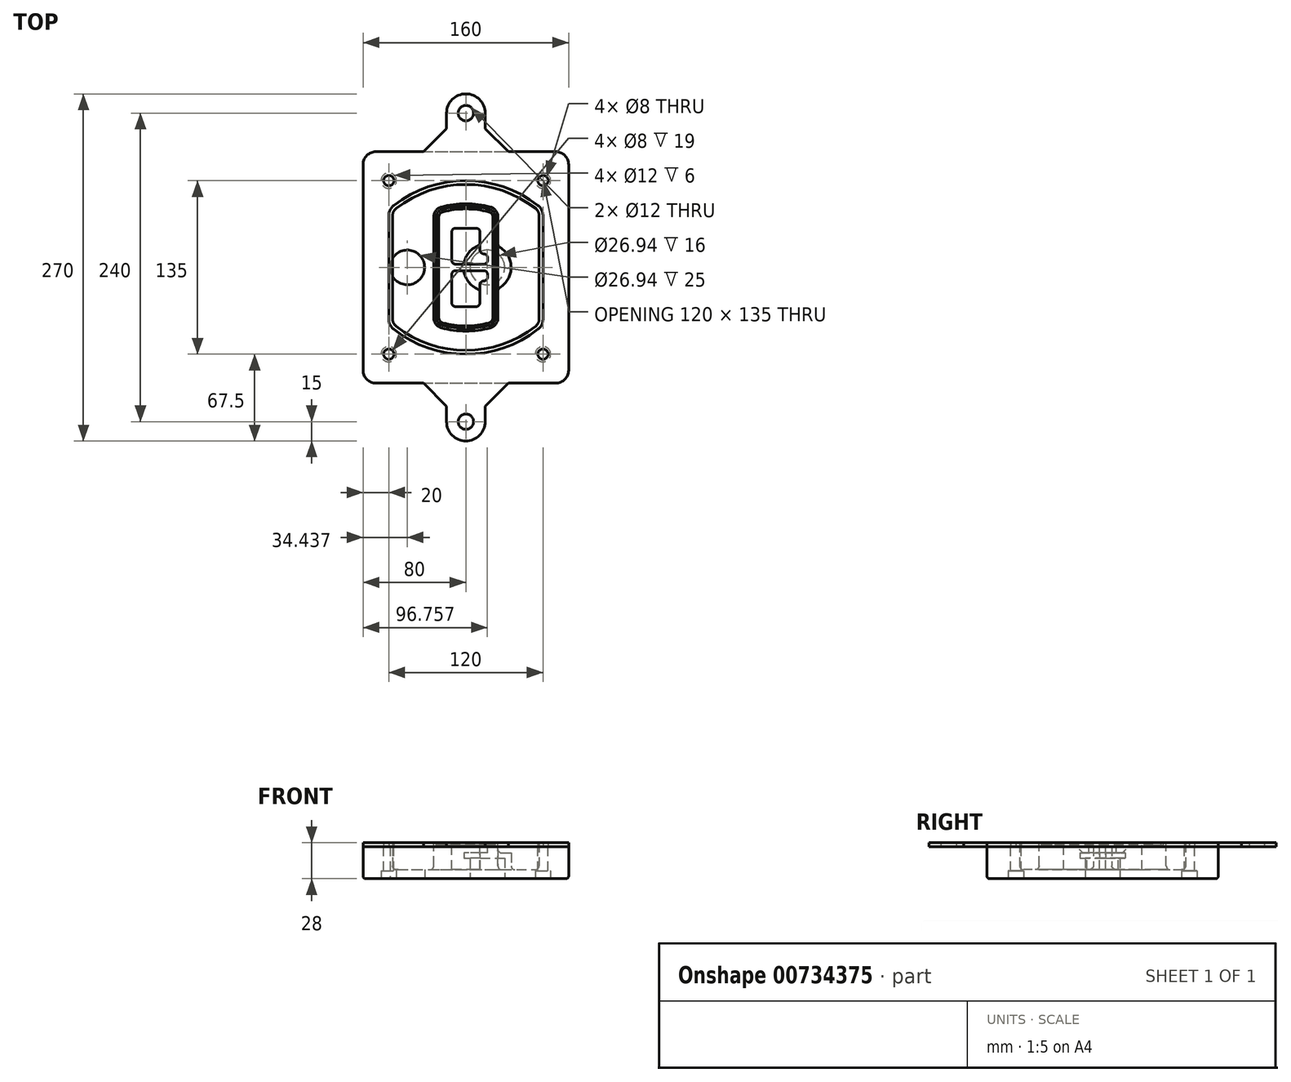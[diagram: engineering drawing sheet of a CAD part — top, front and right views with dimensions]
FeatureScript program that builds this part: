
annotation { "Feature Type Name" : "Feature", "Feature Type Description" : "" }
export const myFeature = defineFeature(function(context is Context, id is Id, definition is map)
    precondition{}
    {
        {
            var Q0;
            Q0=qCreatedBy(makeId("Top.planeOp"),FACE);
            var sketch = newSketch(context, id + "F0", { "sketchPlane" : qUnion([Q0])});
            skPoint(sketch, "E0.rect.middle", {"position": v(0, 0) * mm});
            skLineSegment(sketch, "E1.bottom", {"start": v(-70, -90) * mm, "end": v(70, -90) * mm});
            skLineSegment(sketch, "E1.top", {"start": v(-70, 90) * mm, "end": v(70, 90) * mm});
            skLineSegment(sketch, "E1.left", {"start": v(-80, -80) * mm, "end": v(-80, 80) * mm});
            skLineSegment(sketch, "E1.right", {"start": v(80, -80) * mm, "end": v(80, 80) * mm});
            skLineSegment(sketch, "E2", {"start": v(-80, 90) * mm, "end": v(80, -90) * mm, "construction": true});
            skLineSegment(sketch, "E3", {"start": v(80, 90) * mm, "end": v(-80, -90) * mm, "construction": true});
            skCircle(sketch, "E4", {"center": v(-60, 67.5) * mm, "radius": 4 * mm});
            skCircle(sketch, "E5", {"center": v(60, 67.5) * mm, "radius": 4 * mm});
            skCircle(sketch, "E6", {"center": v(60, -67.5) * mm, "radius": 4 * mm});
            skCircle(sketch, "E7", {"center": v(-60, -67.5) * mm, "radius": 4 * mm});
            skLineSegment(sketch, "E8", {"start": v(-60, 67.5) * mm, "end": v(60, 67.5) * mm, "construction": true});
            skLineSegment(sketch, "E9", {"start": v(60, 67.5) * mm, "end": v(60, -67.5) * mm, "construction": true});
            skLineSegment(sketch, "E10", {"start": v(60, -67.5) * mm, "end": v(-60, -67.5) * mm, "construction": true});
            skLineSegment(sketch, "E11", {"start": v(-60, -67.5) * mm, "end": v(-60, 67.5) * mm, "construction": true});
            skLineSegment(sketch, "E12", {"start": v(-60, 40.3) * mm, "end": v(-60, -40.3) * mm});
            skLineSegment(sketch, "E13", {"start": v(60, 40.3) * mm, "end": v(60, -40.3) * mm});
            skArc(sketch, "E14", {"start": v(56.15, 48.18) * mm, "mid": v(0, 67.5) * mm, "end": v(-56.15, 48.18) * mm});
            skArc(sketch, "E15", {"start": v(-56.15, -48.18) * mm, "mid": v(0, -67.5) * mm, "end": v(56.15, -48.18) * mm});
            skLineSegment(sketch, "E16", {"start": v(-60, 0) * mm, "end": v(60, 0) * mm, "construction": true});
            skPoint(sketch, "E17.visualSharp", {"position": v(-60, -45) * mm});
            skArc(sketch, "E17.filletArc", {"start": v(-60, -40.3) * mm, "mid": v(-58.99, -44.68) * mm, "end": v(-56.15, -48.18) * mm});
            skPoint(sketch, "E18.visualSharp", {"position": v(-60, 45) * mm});
            skArc(sketch, "E18.filletArc", {"start": v(-56.15, 48.18) * mm, "mid": v(-58.99, 44.68) * mm, "end": v(-60, 40.3) * mm});
            skPoint(sketch, "E19.visualSharp", {"position": v(60, 45) * mm});
            skArc(sketch, "E19.filletArc", {"start": v(60, 40.3) * mm, "mid": v(58.99, 44.68) * mm, "end": v(56.15, 48.18) * mm});
            skPoint(sketch, "E20.visualSharp", {"position": v(60, -45) * mm});
            skArc(sketch, "E20.filletArc", {"start": v(56.15, -48.18) * mm, "mid": v(58.99, -44.68) * mm, "end": v(60, -40.3) * mm});
            skPoint(sketch, "E21.visualSharp", {"position": v(-80, 90) * mm});
            skArc(sketch, "E21.filletArc", {"start": v(-70, 90) * mm, "mid": v(-77.07, 87.07) * mm, "end": v(-80, 80) * mm});
            skPoint(sketch, "E22.visualSharp", {"position": v(80, 90) * mm});
            skArc(sketch, "E22.filletArc", {"start": v(80, 80) * mm, "mid": v(77.07, 87.07) * mm, "end": v(70, 90) * mm});
            skPoint(sketch, "E23.visualSharp", {"position": v(80, -90) * mm});
            skArc(sketch, "E23.filletArc", {"start": v(70, -90) * mm, "mid": v(77.07, -87.07) * mm, "end": v(80, -80) * mm});
            skPoint(sketch, "E24.visualSharp", {"position": v(-80, -90) * mm});
            skArc(sketch, "E24.filletArc", {"start": v(-80, -80) * mm, "mid": v(-77.07, -87.07) * mm, "end": v(-70, -90) * mm});
            skArc(sketch, "E25.0", {"start": v(57, 40.3) * mm, "mid": v(56.3, 43.36) * mm, "end": v(54.3, 45.81) * mm});
            skLineSegment(sketch, "E25.1", {"start": v(57, 40.3) * mm, "end": v(57, -40.3) * mm});
            skArc(sketch, "E25.2", {"start": v(54.3, -45.81) * mm, "mid": v(56.3, -43.36) * mm, "end": v(57, -40.3) * mm});
            skArc(sketch, "E25.3", {"start": v(-54.3, -45.81) * mm, "mid": v(0, -64.5) * mm, "end": v(54.3, -45.81) * mm});
            skArc(sketch, "E25.4", {"start": v(-57, -40.3) * mm, "mid": v(-56.3, -43.36) * mm, "end": v(-54.3, -45.81) * mm});
            skArc(sketch, "E25.5", {"start": v(54.3, 45.81) * mm, "mid": v(0, 64.5) * mm, "end": v(-54.3, 45.81) * mm});
            skLineSegment(sketch, "E25.6", {"start": v(-57, 40.3) * mm, "end": v(-57, -40.3) * mm});
            skArc(sketch, "E25.7", {"start": v(-54.3, 45.81) * mm, "mid": v(-56.3, 43.36) * mm, "end": v(-57, 40.3) * mm});
            skArc(sketch, "E26.0", {"start": v(-58.62, 51.33) * mm, "mid": v(-62.58, 46.43) * mm, "end": v(-64, 40.3) * mm});
            skArc(sketch, "E26.1", {"start": v(58.62, 51.33) * mm, "mid": v(0, 71.5) * mm, "end": v(-58.62, 51.33) * mm});
            skArc(sketch, "E26.2", {"start": v(64, 40.3) * mm, "mid": v(62.58, 46.43) * mm, "end": v(58.62, 51.33) * mm});
            skLineSegment(sketch, "E26.3", {"start": v(64, 40.3) * mm, "end": v(64, -40.3) * mm});
            skArc(sketch, "E26.4", {"start": v(58.62, -51.33) * mm, "mid": v(62.58, -46.43) * mm, "end": v(64, -40.3) * mm});
            skLineSegment(sketch, "E26.5", {"start": v(-64, 40.3) * mm, "end": v(-64, -40.3) * mm});
            skArc(sketch, "E26.6", {"start": v(-58.62, -51.33) * mm, "mid": v(0, -71.5) * mm, "end": v(58.62, -51.33) * mm});
            skArc(sketch, "E26.7", {"start": v(-64, -40.3) * mm, "mid": v(-62.58, -46.43) * mm, "end": v(-58.62, -51.33) * mm});
            skSolve(sketch);
        }
        {
            var Q0;
            Q0=makeQuery(id+"F0.imprint","IMPRINT",FACE,{"disambiguationData":[TD([[makeQuery(id+"F0.imprint","IMPRINT",EDGE,{"derivedFrom":sQuery(id+"F0.wireOp",EDGE,"E1.bottom")}),1.0]])]});
            var Q1;
            Q1=makeQuery(id+"F0.imprint","IMPRINT",FACE,{"disambiguationData":[TD([[makeQuery(id+"F0.imprint","IMPRINT",EDGE,{"derivedFrom":sQuery(id+"F0.wireOp",EDGE,"E12")}),1.0]])]});
            var Q2;
            Q2=makeQuery(id+"F0.imprint","IMPRINT",FACE,{"disambiguationData":[TD([[makeQuery(id+"F0.imprint","IMPRINT",EDGE,{"derivedFrom":sQuery(id+"F0.wireOp",EDGE,"E25.0")}),1.0]])]});
            var Q3;
            Q3=makeQuery(id+"F0.imprint","IMPRINT",FACE,{"disambiguationData":[TD([[makeQuery(id+"F0.imprint","IMPRINT",EDGE,{"derivedFrom":sQuery(id+"F0.wireOp",EDGE,"E12")}),-1.0]])]});
            extrude(context, id + "F1", {"entities" : qUnion([Q0, Q1, Q2, Q3]), "oppositeDirection" : true, "depth" : 25 * mm});
        }
        {
            var Q0;
            Q0=makeQuery(id+"F0.imprint","IMPRINT",FACE,{"disambiguationData":[TD([[makeQuery(id+"F0.imprint","IMPRINT",EDGE,{"derivedFrom":sQuery(id+"F0.wireOp",EDGE,"E12")}),1.0]])]});
            extrude(context, id + "F2", {"entities" : qUnion([Q0]), "operationType" : NewBodyOperationType.ADD, "depth" : 3 * mm});
        }
        {
            var Q0;
            Q0=makeQuery(id+"F0.imprint","IMPRINT",FACE,{"disambiguationData":[TD([[makeQuery(id+"F0.imprint","IMPRINT",EDGE,{"derivedFrom":sQuery(id+"F0.wireOp",EDGE,"E25.0")}),1.0]])]});
            extrude(context, id + "F3", {"entities" : qUnion([Q0]), "operationType" : NewBodyOperationType.REMOVE, "oppositeDirection" : true, "depth" : 18 * mm});
        }
        {
            var Q0;
            Q0=makeQuery(id+"F2.opExtrude","CAP_FACE",FACE,{"disambiguationData":[OSD([sQuery(id+"F0.wireOp",EDGE,"E12"),sQuery(id+"F0.wireOp",EDGE,"E13"),sQuery(id+"F0.wireOp",EDGE,"E14"),sQuery(id+"F0.wireOp",EDGE,"E15"),sQuery(id+"F0.wireOp",EDGE,"E17.filletArc"),sQuery(id+"F0.wireOp",EDGE,"E18.filletArc"),sQuery(id+"F0.wireOp",EDGE,"E19.filletArc"),sQuery(id+"F0.wireOp",EDGE,"E20.filletArc"),sQuery(id+"F0.wireOp",EDGE,"E25.0"),sQuery(id+"F0.wireOp",EDGE,"E25.1"),sQuery(id+"F0.wireOp",EDGE,"E25.2"),sQuery(id+"F0.wireOp",EDGE,"E25.3"),sQuery(id+"F0.wireOp",EDGE,"E25.4"),sQuery(id+"F0.wireOp",EDGE,"E25.5"),sQuery(id+"F0.wireOp",EDGE,"E25.6"),sQuery(id+"F0.wireOp",EDGE,"E25.7")])],"isStart":false});
            var sketch = newSketch(context, id + "F4", { "sketchPlane" : qUnion([Q0])});
            skArc(sketch, "E27.0", {"start": v(-19.08, -46.97) * mm, "mid": v(0, -49.5) * mm, "end": v(19.08, -46.97) * mm});
            skArc(sketch, "E28.0", {"start": v(19.08, 46.97) * mm, "mid": v(0, 49.5) * mm, "end": v(-19.08, 46.97) * mm});
            skLineSegment(sketch, "E29", {"start": v(-25, 39.25) * mm, "end": v(-25, -39.25) * mm});
            skLineSegment(sketch, "E30", {"start": v(25, 39.25) * mm, "end": v(25, -39.25) * mm});
            skLineSegment(sketch, "E31", {"start": v(-25, 45.1) * mm, "end": v(25, 45.1) * mm, "construction": true});
            skLineSegment(sketch, "E32", {"start": v(-25, -45.1) * mm, "end": v(25, -45.1) * mm, "construction": true});
            skPoint(sketch, "E33.visualSharp", {"position": v(-25, 45.1) * mm});
            skArc(sketch, "E33.filletArc", {"start": v(-19.08, 46.97) * mm, "mid": v(-23.35, 44.11) * mm, "end": v(-25, 39.25) * mm});
            skPoint(sketch, "E34.visualSharp", {"position": v(25, 45.1) * mm});
            skArc(sketch, "E34.filletArc", {"start": v(25, 39.25) * mm, "mid": v(23.35, 44.11) * mm, "end": v(19.08, 46.97) * mm});
            skPoint(sketch, "E35.visualSharp", {"position": v(25, -45.1) * mm});
            skArc(sketch, "E35.filletArc", {"start": v(19.08, -46.97) * mm, "mid": v(23.35, -44.11) * mm, "end": v(25, -39.25) * mm});
            skPoint(sketch, "E36.visualSharp", {"position": v(-25, -45.1) * mm});
            skArc(sketch, "E36.filletArc", {"start": v(-25, -39.25) * mm, "mid": v(-23.35, -44.11) * mm, "end": v(-19.08, -46.97) * mm});
            skArc(sketch, "E37.0", {"start": v(54.3, 45.81) * mm, "mid": v(0, 64.5) * mm, "end": v(-54.3, 45.81) * mm});
            skArc(sketch, "E37.1", {"start": v(-54.3, 45.81) * mm, "mid": v(-56.3, 43.36) * mm, "end": v(-57, 40.3) * mm});
            skLineSegment(sketch, "E37.2", {"start": v(-57, 40.3) * mm, "end": v(-57, -40.3) * mm});
            skArc(sketch, "E37.3", {"start": v(-57, -40.3) * mm, "mid": v(-56.3, -43.36) * mm, "end": v(-54.3, -45.81) * mm});
            skArc(sketch, "E37.4", {"start": v(-54.3, -45.81) * mm, "mid": v(0, -64.5) * mm, "end": v(54.3, -45.81) * mm});
            skArc(sketch, "E37.5", {"start": v(54.3, -45.81) * mm, "mid": v(56.3, -43.36) * mm, "end": v(57, -40.3) * mm});
            skLineSegment(sketch, "E37.6", {"start": v(57, 40.3) * mm, "end": v(57, -40.3) * mm});
            skArc(sketch, "E37.7", {"start": v(57, 40.3) * mm, "mid": v(56.3, 43.36) * mm, "end": v(54.3, 45.81) * mm});
            skLineSegment(sketch, "E38.0", {"start": v(23, 39.25) * mm, "end": v(23, -39.25) * mm});
            skArc(sketch, "E38.1", {"start": v(18.56, -45.04) * mm, "mid": v(21.76, -42.9) * mm, "end": v(23, -39.25) * mm});
            skArc(sketch, "E38.2", {"start": v(-18.56, -45.04) * mm, "mid": v(0, -47.5) * mm, "end": v(18.56, -45.04) * mm});
            skArc(sketch, "E38.3", {"start": v(-23, -39.25) * mm, "mid": v(-21.76, -42.9) * mm, "end": v(-18.56, -45.04) * mm});
            skLineSegment(sketch, "E38.4", {"start": v(-23, 39.25) * mm, "end": v(-23, -39.25) * mm});
            skArc(sketch, "E38.5", {"start": v(23, 39.25) * mm, "mid": v(21.76, 42.9) * mm, "end": v(18.56, 45.04) * mm});
            skArc(sketch, "E38.6", {"start": v(-18.56, 45.04) * mm, "mid": v(-21.76, 42.9) * mm, "end": v(-23, 39.25) * mm});
            skArc(sketch, "E38.7", {"start": v(18.56, 45.04) * mm, "mid": v(0, 47.5) * mm, "end": v(-18.56, 45.04) * mm});
            skArc(sketch, "E39.0", {"start": v(21, 39.25) * mm, "mid": v(20.18, 41.68) * mm, "end": v(18.04, 43.1) * mm});
            skLineSegment(sketch, "E39.1", {"start": v(21, 39.25) * mm, "end": v(21, -39.25) * mm});
            skArc(sketch, "E39.2", {"start": v(18.04, -43.1) * mm, "mid": v(20.18, -41.68) * mm, "end": v(21, -39.25) * mm});
            skArc(sketch, "E39.3", {"start": v(-18.04, -43.1) * mm, "mid": v(0, -45.5) * mm, "end": v(18.04, -43.1) * mm});
            skArc(sketch, "E39.4", {"start": v(-21, -39.25) * mm, "mid": v(-20.18, -41.68) * mm, "end": v(-18.04, -43.1) * mm});
            skArc(sketch, "E39.5", {"start": v(18.04, 43.1) * mm, "mid": v(0, 45.5) * mm, "end": v(-18.04, 43.1) * mm});
            skLineSegment(sketch, "E39.6", {"start": v(-21, 39.25) * mm, "end": v(-21, -39.25) * mm});
            skArc(sketch, "E39.7", {"start": v(-18.04, 43.1) * mm, "mid": v(-20.18, 41.68) * mm, "end": v(-21, 39.25) * mm});
            skLineSegment(sketch, "E40", {"start": v(-25, 0) * mm, "end": v(25, 0) * mm, "construction": true});
            skLineSegment(sketch, "E41", {"start": v(-11, 5.5) * mm, "end": v(-11, 27.5) * mm});
            skLineSegment(sketch, "E42", {"start": v(-8, 30.5) * mm, "end": v(8, 30.5) * mm});
            skLineSegment(sketch, "E43", {"start": v(11, 27.5) * mm, "end": v(11, 13.5) * mm});
            skLineSegment(sketch, "E44", {"start": v(14, 10.5) * mm, "end": v(14, 10.5) * mm});
            skLineSegment(sketch, "E45", {"start": v(17, 7.5) * mm, "end": v(17, 5.5) * mm});
            skLineSegment(sketch, "E46", {"start": v(14, 2.5) * mm, "end": v(-8, 2.5) * mm});
            skPoint(sketch, "E47.visualSharp", {"position": v(-11, 30.5) * mm});
            skArc(sketch, "E47.filletArc", {"start": v(-8, 30.5) * mm, "mid": v(-10.12, 29.62) * mm, "end": v(-11, 27.5) * mm});
            skPoint(sketch, "E48.visualSharp", {"position": v(11, 30.5) * mm});
            skArc(sketch, "E48.filletArc", {"start": v(11, 27.5) * mm, "mid": v(10.12, 29.62) * mm, "end": v(8, 30.5) * mm});
            skPoint(sketch, "E49.visualSharp", {"position": v(11, 10.5) * mm});
            skArc(sketch, "E49.filletArc", {"start": v(11, 13.5) * mm, "mid": v(11.88, 11.38) * mm, "end": v(14, 10.5) * mm});
            skPoint(sketch, "E50.visualSharp", {"position": v(17, 10.5) * mm});
            skArc(sketch, "E50.filletArc", {"start": v(17, 7.5) * mm, "mid": v(16.12, 9.62) * mm, "end": v(14, 10.5) * mm});
            skPoint(sketch, "E51.visualSharp", {"position": v(17, 2.5) * mm});
            skArc(sketch, "E51.filletArc", {"start": v(14, 2.5) * mm, "mid": v(16.12, 3.38) * mm, "end": v(17, 5.5) * mm});
            skPoint(sketch, "E52.visualSharp", {"position": v(-11, 2.5) * mm});
            skArc(sketch, "E52.filletArc", {"start": v(-11, 5.5) * mm, "mid": v(-10.12, 3.38) * mm, "end": v(-8, 2.5) * mm});
            skLineSegment(sketch, "E53.0.MirrorCS", {"start": v(14, -2.5) * mm, "end": v(-8, -2.5) * mm});
            skArc(sketch, "E54.0.MirrorCS", {"start": v(-11, -5.5) * mm, "mid": v(-10.12, -3.38) * mm, "end": v(-8, -2.5) * mm});
            skLineSegment(sketch, "E55.0.MirrorCS", {"start": v(-11, -5.5) * mm, "end": v(-11, -27.5) * mm});
            skArc(sketch, "E56.0.MirrorCS", {"start": v(-8, -30.5) * mm, "mid": v(-10.12, -29.62) * mm, "end": v(-11, -27.5) * mm});
            skLineSegment(sketch, "E57.0.MirrorCS", {"start": v(-8, -30.5) * mm, "end": v(8, -30.5) * mm});
            skArc(sketch, "E58.0.MirrorCS", {"start": v(11, -27.5) * mm, "mid": v(10.12, -29.62) * mm, "end": v(8, -30.5) * mm});
            skLineSegment(sketch, "E59.0.MirrorCS", {"start": v(11, -27.5) * mm, "end": v(11, -13.5) * mm});
            skArc(sketch, "E60.0.MirrorCS", {"start": v(11, -13.5) * mm, "mid": v(11.88, -11.38) * mm, "end": v(14, -10.5) * mm});
            skArc(sketch, "E61.0.MirrorCS", {"start": v(17, -7.5) * mm, "mid": v(16.12, -9.62) * mm, "end": v(14, -10.5) * mm});
            skLineSegment(sketch, "E62.0.MirrorCS", {"start": v(17, -7.5) * mm, "end": v(17, -5.5) * mm});
            skArc(sketch, "E63.0.MirrorCS", {"start": v(14, -2.5) * mm, "mid": v(16.12, -3.38) * mm, "end": v(17, -5.5) * mm});
            skSolve(sketch);
        }
        {
            var Q0;
            Q0=makeQuery(id+"F4.imprint","IMPRINT",FACE,{"disambiguationData":[TD([[makeQuery(id+"F4.imprint","IMPRINT",EDGE,{"derivedFrom":sQuery(id+"F4.wireOp",EDGE,"E27.0")}),1.0]])]});
            var Q1;
            Q1=makeQuery(id+"F4.imprint","IMPRINT",FACE,{"disambiguationData":[TD([[makeQuery(id+"F4.imprint","IMPRINT",EDGE,{"derivedFrom":sQuery(id+"F4.wireOp",EDGE,"E38.0")}),-1.0]])]});
            var Q2;
            Q2=makeQuery(id+"F4.imprint","IMPRINT",FACE,{"disambiguationData":[TD([[makeQuery(id+"F4.imprint","IMPRINT",EDGE,{"derivedFrom":sQuery(id+"F4.wireOp",EDGE,"E39.0")}),1.0]])]});
            extrude(context, id + "F5", {"entities" : qUnion([Q0, Q1, Q2]), "operationType" : NewBodyOperationType.ADD, "endBound" : BoundingType.UP_TO_NEXT, "oppositeDirection" : true, "depth" : 25 * mm});
        }
        {
            var Q0;
            Q0=makeQuery(id+"F4.imprint","IMPRINT",FACE,{"disambiguationData":[TD([[makeQuery(id+"F4.imprint","IMPRINT",EDGE,{"derivedFrom":sQuery(id+"F4.wireOp",EDGE,"E38.0")}),-1.0]])]});
            extrude(context, id + "F6", {"entities" : qUnion([Q0]), "operationType" : NewBodyOperationType.REMOVE, "oppositeDirection" : true, "depth" : 2 * mm});
        }
        {
            var Q0;
            Q0=makeQuery(id+"F1.opExtrude","CAP_FACE",FACE,{"disambiguationData":[OSD([sQuery(id+"F0.wireOp",EDGE,"E1.bottom"),sQuery(id+"F0.wireOp",EDGE,"E1.top"),sQuery(id+"F0.wireOp",EDGE,"E1.left"),sQuery(id+"F0.wireOp",EDGE,"E1.right"),sQuery(id+"F0.wireOp",EDGE,"E4"),sQuery(id+"F0.wireOp",EDGE,"E5"),sQuery(id+"F0.wireOp",EDGE,"E6"),sQuery(id+"F0.wireOp",EDGE,"E7"),sQuery(id+"F0.wireOp",EDGE,"E21.filletArc"),sQuery(id+"F0.wireOp",EDGE,"E22.filletArc"),sQuery(id+"F0.wireOp",EDGE,"E23.filletArc"),sQuery(id+"F0.wireOp",EDGE,"E24.filletArc")])],"isStart":false});
            var sketch = newSketch(context, id + "F7", { "sketchPlane" : qUnion([Q0])});
            skCircle(sketch, "E64", {"center": v(16.76, 0) * mm, "radius": 13.47 * mm});
            skCircle(sketch, "E65", {"center": v(-45.56, 0) * mm, "radius": 13.47 * mm});
            skLineSegment(sketch, "E66", {"start": v(80, 0) * mm, "end": v(-80, 0) * mm});
            skCircle(sketch, "E67", {"center": v(16.76, 0) * mm, "radius": 18.47 * mm});
            skCircle(sketch, "E68", {"center": v(60, -67.5) * mm, "radius": 6 * mm});
            skCircle(sketch, "E69", {"center": v(-60, -67.5) * mm, "radius": 6 * mm});
            skCircle(sketch, "E70", {"center": v(-60, 67.5) * mm, "radius": 6 * mm});
            skCircle(sketch, "E71", {"center": v(60, 67.5) * mm, "radius": 6 * mm});
            skSolve(sketch);
        }
        {
            var Q0;
            {var subQ1=sQuery(id+"F7.wireOp",EDGE,"E66");var subQ4=sQuery(id+"F7.wireOp",EDGE,"E64");var subQ6=makeQuery(id+"F7.imprint","INTERSECT",VERTEX,{"disambiguationData":[OD(0.0)],"derivedFrom":[subQ4,subQ1]});Q0=makeQuery(id+"F7.imprint","IMPRINT",FACE,{"disambiguationData":[TD([[makeQuery(id+"F7.imprint","IMPRINT",EDGE,{"disambiguationData":[TD([[subQ6,-1.0]])],"derivedFrom":subQ4}),-1.0]])]});}
            var Q1;
            {var subQ0=sQuery(id+"F7.wireOp",EDGE,"E66");var subQ1=sQuery(id+"F7.wireOp",EDGE,"E64");var subQ3=makeQuery(id+"F7.imprint","INTERSECT",VERTEX,{"disambiguationData":[OD(0.0)],"derivedFrom":[subQ1,subQ0]});Q1=makeQuery(id+"F7.imprint","IMPRINT",FACE,{"disambiguationData":[TD([[makeQuery(id+"F7.imprint","IMPRINT",EDGE,{"disambiguationData":[TD([[subQ3,-1.0]])],"derivedFrom":subQ1}),1.0]])]});}
            var Q2;
            {var subQ0=sQuery(id+"F7.wireOp",EDGE,"E66");var subQ1=sQuery(id+"F7.wireOp",EDGE,"E64");var subQ3=makeQuery(id+"F7.imprint","INTERSECT",VERTEX,{"disambiguationData":[OD(0.0)],"derivedFrom":[subQ1,subQ0]});Q2=makeQuery(id+"F7.imprint","IMPRINT",FACE,{"disambiguationData":[TD([[makeQuery(id+"F7.imprint","IMPRINT",EDGE,{"disambiguationData":[TD([[subQ3,1.0]])],"derivedFrom":subQ1}),1.0]])]});}
            var Q3;
            {var subQ1=sQuery(id+"F7.wireOp",EDGE,"E66");var subQ4=sQuery(id+"F7.wireOp",EDGE,"E64");var subQ6=makeQuery(id+"F7.imprint","INTERSECT",VERTEX,{"disambiguationData":[OD(0.0)],"derivedFrom":[subQ4,subQ1]});Q3=makeQuery(id+"F7.imprint","IMPRINT",FACE,{"disambiguationData":[TD([[makeQuery(id+"F7.imprint","IMPRINT",EDGE,{"disambiguationData":[TD([[subQ6,1.0]])],"derivedFrom":subQ4}),-1.0]])]});}
            extrude(context, id + "F8", {"entities" : qUnion([Q0, Q1, Q2, Q3]), "operationType" : NewBodyOperationType.ADD, "oppositeDirection" : true, "depth" : 20 * mm});
        }
        {
            var Q0;
            {var subQ0=sQuery(id+"F7.wireOp",EDGE,"E66");var subQ1=sQuery(id+"F7.wireOp",EDGE,"E64");var subQ3=makeQuery(id+"F7.imprint","INTERSECT",VERTEX,{"disambiguationData":[OD(0.0)],"derivedFrom":[subQ1,subQ0]});Q0=makeQuery(id+"F7.imprint","IMPRINT",FACE,{"disambiguationData":[TD([[makeQuery(id+"F7.imprint","IMPRINT",EDGE,{"disambiguationData":[TD([[subQ3,-1.0]])],"derivedFrom":subQ1}),1.0]])]});}
            var Q1;
            {var subQ0=sQuery(id+"F7.wireOp",EDGE,"E66");var subQ1=sQuery(id+"F7.wireOp",EDGE,"E64");var subQ3=makeQuery(id+"F7.imprint","INTERSECT",VERTEX,{"disambiguationData":[OD(0.0)],"derivedFrom":[subQ1,subQ0]});Q1=makeQuery(id+"F7.imprint","IMPRINT",FACE,{"disambiguationData":[TD([[makeQuery(id+"F7.imprint","IMPRINT",EDGE,{"disambiguationData":[TD([[subQ3,1.0]])],"derivedFrom":subQ1}),1.0]])]});}
            extrude(context, id + "F9", {"entities" : qUnion([Q0, Q1]), "operationType" : NewBodyOperationType.REMOVE, "oppositeDirection" : true, "depth" : 16 * mm});
        }
        {
            var Q0;
            {var subQ0=sQuery(id+"F7.wireOp",EDGE,"E66");var subQ1=sQuery(id+"F7.wireOp",EDGE,"E65");var subQ3=makeQuery(id+"F7.imprint","INTERSECT",VERTEX,{"disambiguationData":[OD(0.0)],"derivedFrom":[subQ1,subQ0]});Q0=makeQuery(id+"F7.imprint","IMPRINT",FACE,{"disambiguationData":[TD([[makeQuery(id+"F7.imprint","IMPRINT",EDGE,{"disambiguationData":[TD([[subQ3,-1.0]])],"derivedFrom":subQ1}),1.0]])]});}
            var Q1;
            {var subQ0=sQuery(id+"F7.wireOp",EDGE,"E66");var subQ1=sQuery(id+"F7.wireOp",EDGE,"E65");var subQ3=makeQuery(id+"F7.imprint","INTERSECT",VERTEX,{"disambiguationData":[OD(0.0)],"derivedFrom":[subQ1,subQ0]});Q1=makeQuery(id+"F7.imprint","IMPRINT",FACE,{"disambiguationData":[TD([[makeQuery(id+"F7.imprint","IMPRINT",EDGE,{"disambiguationData":[TD([[subQ3,1.0]])],"derivedFrom":subQ1}),1.0]])]});}
            extrude(context, id + "F10", {"entities" : qUnion([Q0, Q1]), "operationType" : NewBodyOperationType.REMOVE, "oppositeDirection" : true, "depth" : 25 * mm});
        }
        {
            var Q0;
            Q0=makeQuery(id+"F7.imprint","IMPRINT",FACE,{"disambiguationData":[TD([[makeQuery(id+"F7.imprint","IMPRINT",EDGE,{"derivedFrom":sQuery(id+"F7.wireOp",EDGE,"E68")}),1.0]])]});
            var Q1;
            Q1=makeQuery(id+"F7.imprint","IMPRINT",FACE,{"disambiguationData":[TD([[makeQuery(id+"F7.imprint","IMPRINT",EDGE,{"derivedFrom":makeQuery(id+"F1.opExtrude","CAP_EDGE",EDGE,{"disambiguationData":[OSD([sQuery(id+"F0.wireOp",EDGE,"E5")])],"isStart":false})}),-1.0]])]});
            var Q2;
            Q2=makeQuery(id+"F7.imprint","IMPRINT",FACE,{"disambiguationData":[TD([[makeQuery(id+"F7.imprint","IMPRINT",EDGE,{"derivedFrom":sQuery(id+"F7.wireOp",EDGE,"E69")}),1.0]])]});
            var Q3;
            Q3=makeQuery(id+"F7.imprint","IMPRINT",FACE,{"disambiguationData":[TD([[makeQuery(id+"F7.imprint","IMPRINT",EDGE,{"derivedFrom":makeQuery(id+"F1.opExtrude","CAP_EDGE",EDGE,{"disambiguationData":[OSD([sQuery(id+"F0.wireOp",EDGE,"E4")])],"isStart":false})}),-1.0]])]});
            var Q4;
            Q4=makeQuery(id+"F7.imprint","IMPRINT",FACE,{"disambiguationData":[TD([[makeQuery(id+"F7.imprint","IMPRINT",EDGE,{"derivedFrom":sQuery(id+"F7.wireOp",EDGE,"E70")}),1.0]])]});
            var Q5;
            Q5=makeQuery(id+"F7.imprint","IMPRINT",FACE,{"disambiguationData":[TD([[makeQuery(id+"F7.imprint","IMPRINT",EDGE,{"derivedFrom":makeQuery(id+"F1.opExtrude","CAP_EDGE",EDGE,{"disambiguationData":[OSD([sQuery(id+"F0.wireOp",EDGE,"E7")])],"isStart":false})}),-1.0]])]});
            var Q6;
            Q6=makeQuery(id+"F7.imprint","IMPRINT",FACE,{"disambiguationData":[TD([[makeQuery(id+"F7.imprint","IMPRINT",EDGE,{"derivedFrom":sQuery(id+"F7.wireOp",EDGE,"E71")}),1.0]])]});
            var Q7;
            Q7=makeQuery(id+"F7.imprint","IMPRINT",FACE,{"disambiguationData":[TD([[makeQuery(id+"F7.imprint","IMPRINT",EDGE,{"derivedFrom":makeQuery(id+"F1.opExtrude","CAP_EDGE",EDGE,{"disambiguationData":[OSD([sQuery(id+"F0.wireOp",EDGE,"E6")])],"isStart":false})}),-1.0]])]});
            extrude(context, id + "F11", {"entities" : qUnion([Q0, Q1, Q2, Q3, Q4, Q5, Q6, Q7]), "operationType" : NewBodyOperationType.REMOVE, "oppositeDirection" : true, "depth" : 6 * mm});
        }
        {
            var Q0;
            Q0=makeQuery(id+"F9.boolean.opBoolean","COPY",FACE,{"derivedFrom":makeQuery(id+"F9.opExtrude","CAP_FACE",FACE,{"disambiguationData":[OSD([sQuery(id+"F7.wireOp",EDGE,"E64")])],"isStart":false})});
            var sketch = newSketch(context, id + "F12", { "sketchPlane" : qUnion([Q0])});
            skArc(sketch, "E72.0", {"start": v(11, 17.55) * mm, "mid": v(2.57, 11.82) * mm, "end": v(-1.54, 2.5) * mm});
            skArc(sketch, "E72.1", {"start": v(-1.54, -2.5) * mm, "mid": v(2.57, -11.82) * mm, "end": v(11, -17.55) * mm});
            skLineSegment(sketch, "E73", {"start": v(-1.54, -2.5) * mm, "end": v(14, -2.5) * mm});
            skLineSegment(sketch, "E74.0", {"start": v(14, 2.5) * mm, "end": v(-1.54, 2.5) * mm});
            skArc(sketch, "E74.1", {"start": v(14, 2.5) * mm, "mid": v(16.12, 3.38) * mm, "end": v(17, 5.5) * mm});
            skLineSegment(sketch, "E74.2", {"start": v(17, 7.5) * mm, "end": v(17, 5.5) * mm});
            skArc(sketch, "E74.3", {"start": v(17, 7.5) * mm, "mid": v(16.12, 9.62) * mm, "end": v(14, 10.5) * mm});
            skArc(sketch, "E74.4", {"start": v(11, 13.5) * mm, "mid": v(11.88, 11.38) * mm, "end": v(14, 10.5) * mm});
            skLineSegment(sketch, "E74.5", {"start": v(11, 17.55) * mm, "end": v(11, 13.5) * mm});
            skLineSegment(sketch, "E74.7", {"start": v(14, -2.5) * mm, "end": v(-1.54, -2.5) * mm});
            skArc(sketch, "E74.8", {"start": v(14, -2.5) * mm, "mid": v(16.12, -3.38) * mm, "end": v(17, -5.5) * mm});
            skLineSegment(sketch, "E74.9", {"start": v(17, -7.5) * mm, "end": v(17, -5.5) * mm});
            skArc(sketch, "E74.10", {"start": v(17, -7.5) * mm, "mid": v(16.12, -9.62) * mm, "end": v(14, -10.5) * mm});
            skArc(sketch, "E74.11", {"start": v(11, -13.5) * mm, "mid": v(11.88, -11.38) * mm, "end": v(14, -10.5) * mm});
            skLineSegment(sketch, "E74.12", {"start": v(11, -17.55) * mm, "end": v(11, -13.5) * mm});
            skPoint(sketch, "E75.orphan", {"position": v(11, -27.5) * mm});
            skPoint(sketch, "E76.orphan", {"position": v(-8, -2.5) * mm});
            skPoint(sketch, "E77.orphan", {"position": v(-8, 2.5) * mm});
            skPoint(sketch, "E78.orphan", {"position": v(11, 27.5) * mm});
            skSolve(sketch);
        }
        {
            var Q0;
            {var subQ7=sQuery(id+"F12.wireOp",EDGE,"E72.0");var subQ14=sQuery(id+"F12.wireOp",EDGE,"E72.1");var subQ16=sQuery(id+"F12.wireOp",EDGE,"E74.1");var subQ18=sQuery(id+"F12.wireOp",EDGE,"E74.8");Q0=qUnion([makeQuery(id+"F12.imprint","IMPRINT",FACE,{"disambiguationData":[TD([[makeQuery(id+"F12.imprint","IMPRINT",EDGE,{"derivedFrom":subQ7}),1.0]])]}),makeQuery(id+"F12.imprint","IMPRINT",FACE,{"disambiguationData":[TD([[makeQuery(id+"F12.imprint","IMPRINT",EDGE,{"derivedFrom":subQ14}),1.0]])]}),makeQuery(id+"F12.imprint","IMPRINT",FACE,{"disambiguationData":[TD([[makeQuery(id+"F12.imprint","IMPRINT",EDGE,{"derivedFrom":subQ16}),1.0]])]}),makeQuery(id+"F12.imprint","IMPRINT",FACE,{"disambiguationData":[TD([[makeQuery(id+"F12.imprint","IMPRINT",EDGE,{"derivedFrom":subQ18}),-1.0]])]})]);}
            var Q1;
            Q1=makeQuery(id+"F5.boolean.opBoolean","SPLIT",FACE,{"disambiguationData":[TD([makeQuery(id+"F5.opExtrude","SWEPT_FACE",FACE,{"disambiguationData":[OSD([sQuery(id+"F4.wireOp",EDGE,"E41")])]})])],"derivedFrom":makeQuery(id+"F3.boolean.opBoolean","COPY",FACE,{"derivedFrom":makeQuery(id+"F3.opExtrude","CAP_FACE",FACE,{"disambiguationData":[OSD([sQuery(id+"F0.wireOp",EDGE,"E25.0"),sQuery(id+"F0.wireOp",EDGE,"E25.1"),sQuery(id+"F0.wireOp",EDGE,"E25.2"),sQuery(id+"F0.wireOp",EDGE,"E25.3"),sQuery(id+"F0.wireOp",EDGE,"E25.4"),sQuery(id+"F0.wireOp",EDGE,"E25.5"),sQuery(id+"F0.wireOp",EDGE,"E25.6"),sQuery(id+"F0.wireOp",EDGE,"E25.7")])],"isStart":false})})});
            extrude(context, id + "F13", {"entities" : qUnion([Q0]), "operationType" : NewBodyOperationType.REMOVE, "endBound" : BoundingType.UP_TO_SURFACE, "endBoundEntityFace" : qUnion([Q1]), "depth" : 25 * mm});
        }
        {
            var Q0;
            Q0=makeQuery(id+"F3.boolean.opBoolean","COPY",EDGE,{"derivedFrom":makeQuery(id+"F3.opExtrude","CAP_EDGE",EDGE,{"disambiguationData":[OSD([sQuery(id+"F0.wireOp",EDGE,"E25.6")])],"isStart":false})});
            var Q1;
            Q1=makeQuery(id+"F8.boolean.opBoolean","INTERSECT",EDGE,{"derivedFrom":[makeQuery(id+"F5.opExtrude","SWEPT_FACE",FACE,{"disambiguationData":[OSD([sQuery(id+"F4.wireOp",EDGE,"E30")])]}),makeQuery(id+"F8.opExtrude","CAP_FACE",FACE,{"disambiguationData":[OSD([sQuery(id+"F7.wireOp",EDGE,"E67")])],"isStart":false})]});
            var Q2;
            Q2=makeQuery(id+"F8.boolean.opBoolean","INTERSECT",EDGE,{"disambiguationData":[OD(1.0)],"derivedFrom":[makeQuery(id+"F5.opExtrude","SWEPT_FACE",FACE,{"disambiguationData":[OSD([sQuery(id+"F4.wireOp",EDGE,"E30")])]}),makeQuery(id+"F8.opExtrude","SWEPT_FACE",FACE,{"disambiguationData":[OSD([sQuery(id+"F7.wireOp",EDGE,"E67")])]})]});
            var Q3;
            {var subQ0=sQuery(id+"F4.wireOp",EDGE,"E30");Q3=makeQuery(id+"F8.boolean.opBoolean","SPLIT",EDGE,{"disambiguationData":[TD([makeQuery(id+"F5.opExtrude","SWEPT_FACE",FACE,{"disambiguationData":[OSD([sQuery(id+"F4.wireOp",EDGE,"E35.filletArc")])]})])],"derivedFrom":makeQuery(id+"F5.opExtrude","CAP_EDGE",EDGE,{"disambiguationData":[OSD([subQ0])],"isStart":false})});}
            var Q4;
            {var subQ0=sQuery(id+"F0.wireOp",EDGE,"E25.7");var subQ1=sQuery(id+"F0.wireOp",EDGE,"E25.1");var subQ2=sQuery(id+"F0.wireOp",EDGE,"E25.6");var subQ3=sQuery(id+"F0.wireOp",EDGE,"E25.5");var subQ4=sQuery(id+"F0.wireOp",EDGE,"E25.4");var subQ5=sQuery(id+"F0.wireOp",EDGE,"E25.0");var subQ6=sQuery(id+"F0.wireOp",EDGE,"E25.2");var subQ7=sQuery(id+"F0.wireOp",EDGE,"E25.3");Q4=makeQuery(id+"F8.boolean.opBoolean","INTERSECT",EDGE,{"derivedFrom":[makeQuery(id+"F5.boolean.opBoolean","SPLIT",FACE,{"disambiguationData":[TD([makeQuery(id+"F2.opExtrude","SWEPT_FACE",FACE,{"disambiguationData":[OSD([subQ5])]})])],"derivedFrom":makeQuery(id+"F3.boolean.opBoolean","COPY",FACE,{"derivedFrom":makeQuery(id+"F3.opExtrude","CAP_FACE",FACE,{"disambiguationData":[OSD([subQ5,subQ1,subQ6,subQ7,subQ4,subQ3,subQ2,subQ0])],"isStart":false})})}),makeQuery(id+"F8.opExtrude","SWEPT_FACE",FACE,{"disambiguationData":[OSD([sQuery(id+"F7.wireOp",EDGE,"E67")])]})]});}
            var Q5;
            Q5=makeQuery(id+"F8.boolean.opBoolean","INTERSECT",EDGE,{"disambiguationData":[OD(0.0)],"derivedFrom":[makeQuery(id+"F5.opExtrude","SWEPT_FACE",FACE,{"disambiguationData":[OSD([sQuery(id+"F4.wireOp",EDGE,"E30")])]}),makeQuery(id+"F8.opExtrude","SWEPT_FACE",FACE,{"disambiguationData":[OSD([sQuery(id+"F7.wireOp",EDGE,"E67")])]})]});
            fillet(context, id + "F14", {"entities" : qUnion([Q0, Q1, Q2, Q3, Q4, Q5]), "radius" : 3 * mm, "tangentPropagation" : true, "allowEdgeOverflow" : false});
        }
        {
            var Q0;
            Q0=makeQuery(id+"F1.opExtrude","CAP_EDGE",EDGE,{"disambiguationData":[OSD([sQuery(id+"F0.wireOp",EDGE,"E1.bottom")])],"isStart":false});
            fillet(context, id + "F15", {"entities" : qUnion([Q0]), "radius" : 2 * mm, "tangentPropagation" : true, "allowEdgeOverflow" : false});
        }
        {
            var Q0;
            {var subQ0=sQuery(id+"F0.wireOp",EDGE,"E21.filletArc");var subQ1=sQuery(id+"F0.wireOp",EDGE,"E7");var subQ2=sQuery(id+"F0.wireOp",EDGE,"E6");var subQ3=sQuery(id+"F0.wireOp",EDGE,"E5");var subQ4=sQuery(id+"F0.wireOp",EDGE,"E4");var subQ5=sQuery(id+"F0.wireOp",EDGE,"E22.filletArc");var subQ6=sQuery(id+"F0.wireOp",EDGE,"E1.bottom");var subQ7=sQuery(id+"F0.wireOp",EDGE,"E1.right");var subQ8=sQuery(id+"F0.wireOp",EDGE,"E1.top");var subQ9=sQuery(id+"F0.wireOp",EDGE,"E1.left");var subQ10=sQuery(id+"F0.wireOp",EDGE,"E23.filletArc");var subQ11=sQuery(id+"F0.wireOp",EDGE,"E24.filletArc");Q0=makeQuery(id+"F2.boolean.opBoolean","SPLIT",FACE,{"disambiguationData":[TD([makeQuery(id+"F1.opExtrude","SWEPT_FACE",FACE,{"disambiguationData":[OSD([subQ6])]})])],"derivedFrom":makeQuery(id+"F1.opExtrude","CAP_FACE",FACE,{"disambiguationData":[OSD([subQ6,subQ8,subQ9,subQ7,subQ4,subQ3,subQ2,subQ1,subQ0,subQ5,subQ10,subQ11])],"isStart":true})});}
            var sketch = newSketch(context, id + "F16", { "sketchPlane" : qUnion([Q0])});
            skCircle(sketch, "E79", {"center": v(0, 120) * mm, "radius": 6 * mm});
            skLineSegment(sketch, "E80", {"start": v(-15, 108) * mm, "end": v(-15, 120) * mm});
            skArc(sketch, "E81", {"start": v(15, 120) * mm, "mid": v(0, 135) * mm, "end": v(-15, 120) * mm});
            skLineSegment(sketch, "E82", {"start": v(15, 120) * mm, "end": v(15, 108) * mm});
            skLineSegment(sketch, "E83", {"start": v(15, 108) * mm, "end": v(33, 90) * mm});
            skLineSegment(sketch, "E84", {"start": v(-15, 108) * mm, "end": v(-33, 90) * mm});
            skLineSegment(sketch, "E85", {"start": v(-80, 0) * mm, "end": v(80, 0) * mm, "construction": true});
            skLineSegment(sketch, "E86.MirrorCS", {"start": v(15, -108) * mm, "end": v(33, -90) * mm});
            skLineSegment(sketch, "E87.MirrorCS", {"start": v(-15, -108) * mm, "end": v(-33, -90) * mm});
            skCircle(sketch, "E88.MirrorC", {"center": v(0, -120) * mm, "radius": 6 * mm});
            skLineSegment(sketch, "E89.MirrorCS", {"start": v(-15, -108) * mm, "end": v(-15, -120) * mm});
            skLineSegment(sketch, "E90.MirrorCS", {"start": v(15, -120) * mm, "end": v(15, -108) * mm});
            skArc(sketch, "E91.MirrorCS", {"start": v(15, -120) * mm, "mid": v(0, -135) * mm, "end": v(-15, -120) * mm});
            skSolve(sketch);
        }
        {
            var Q0;
            Q0=makeQuery(id+"F16.imprint","IMPRINT",FACE,{"disambiguationData":[TD([[makeQuery(id+"F16.imprint","IMPRINT",EDGE,{"derivedFrom":sQuery(id+"F16.wireOp",EDGE,"E79")}),-1.0]])]});
            var Q1;
            Q1=makeQuery(id+"F16.imprint","IMPRINT",FACE,{"disambiguationData":[TD([[makeQuery(id+"F16.imprint","IMPRINT",EDGE,{"derivedFrom":makeQuery(id+"F1.opExtrude","CAP_EDGE",EDGE,{"disambiguationData":[OSD([sQuery(id+"F0.wireOp",EDGE,"E1.left")])],"isStart":true})}),-1.0]])]});
            var Q2;
            {var subQ1=sQuery(id+"F16.wireOp",EDGE,"E86.MirrorCS");Q2=makeQuery(id+"F16.imprint","IMPRINT",FACE,{"disambiguationData":[TD([[makeQuery(id+"F16.imprint","IMPRINT",EDGE,{"derivedFrom":subQ1}),1.0]])]});}
            var Q3;
            Q3 = qConstructionFilter(qBodyType(qCreatedBy(id + "F16" ,EDGE), BodyType.WIRE), ConstructionObject.NO);
            var Q4;
            Q4=makeQuery(id+"F2.opExtrude","CAP_FACE",FACE,{"disambiguationData":[OSD([sQuery(id+"F0.wireOp",EDGE,"E12"),sQuery(id+"F0.wireOp",EDGE,"E13"),sQuery(id+"F0.wireOp",EDGE,"E14"),sQuery(id+"F0.wireOp",EDGE,"E15"),sQuery(id+"F0.wireOp",EDGE,"E17.filletArc"),sQuery(id+"F0.wireOp",EDGE,"E18.filletArc"),sQuery(id+"F0.wireOp",EDGE,"E19.filletArc"),sQuery(id+"F0.wireOp",EDGE,"E20.filletArc"),sQuery(id+"F0.wireOp",EDGE,"E25.0"),sQuery(id+"F0.wireOp",EDGE,"E25.1"),sQuery(id+"F0.wireOp",EDGE,"E25.2"),sQuery(id+"F0.wireOp",EDGE,"E25.3"),sQuery(id+"F0.wireOp",EDGE,"E25.4"),sQuery(id+"F0.wireOp",EDGE,"E25.5"),sQuery(id+"F0.wireOp",EDGE,"E25.6"),sQuery(id+"F0.wireOp",EDGE,"E25.7")])],"isStart":false});
            extrude(context, id + "F17", {"entities" : qUnion([Q0, Q1, Q2]), "surfaceEntities" : qUnion([Q3]), "endBound" : BoundingType.UP_TO_SURFACE, "depth" : 25 * mm, "endBoundEntityFace" : qUnion([Q4]), "offsetDistance" : 25 * mm});
        }
    });
